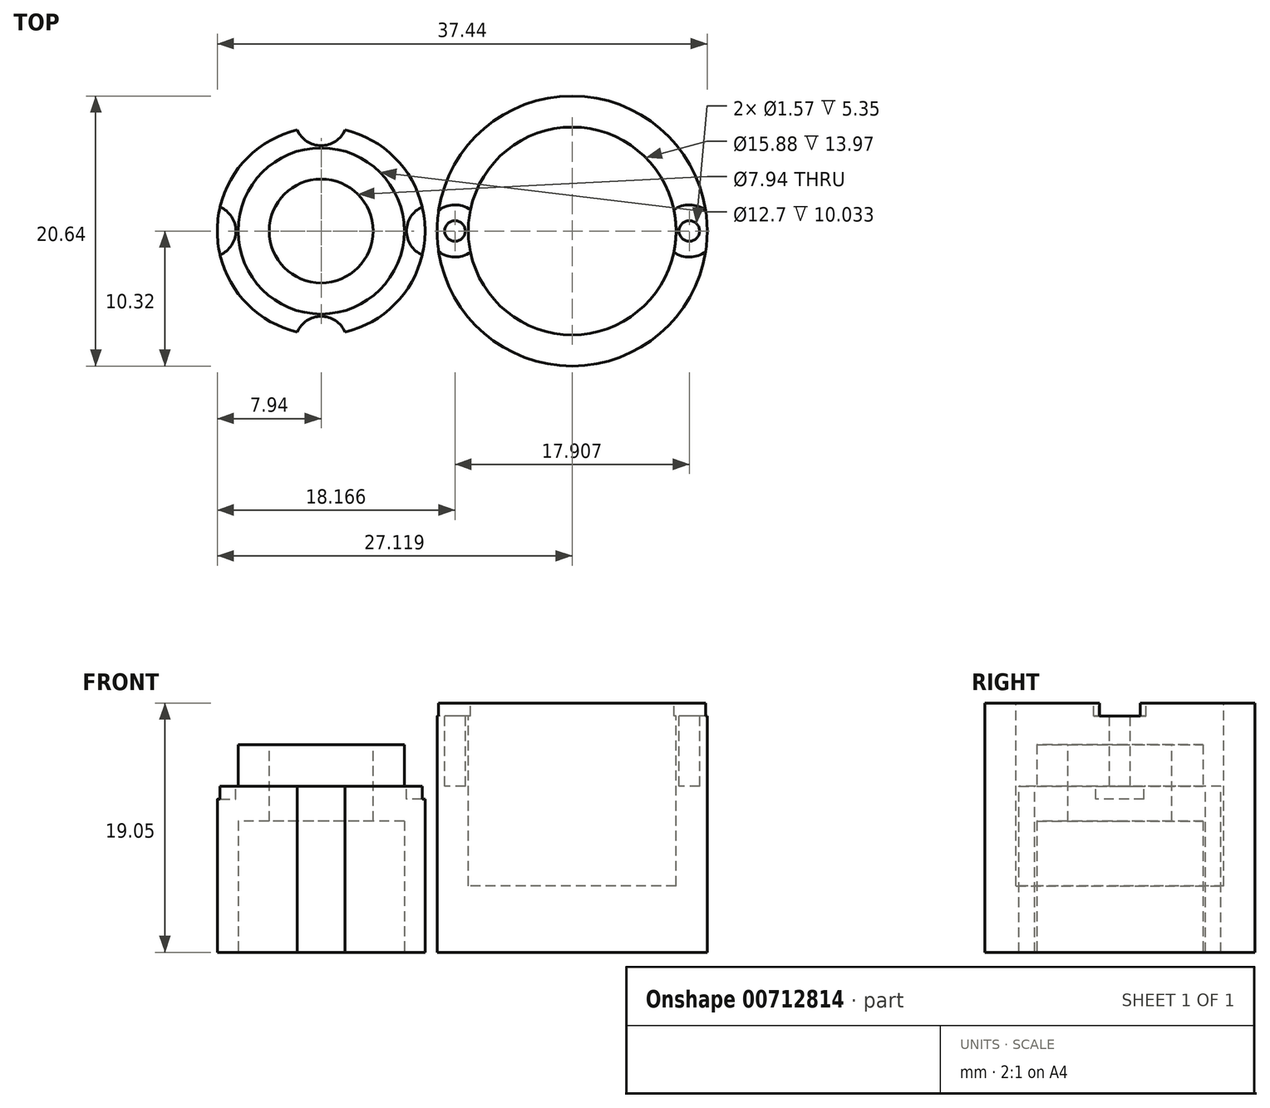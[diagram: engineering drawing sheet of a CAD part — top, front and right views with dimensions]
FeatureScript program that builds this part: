
annotation { "Feature Type Name" : "Feature", "Feature Type Description" : "" }
export const myFeature = defineFeature(function(context is Context, id is Id, definition is map)
    precondition{}
    {
        {
            var Q0;
            Q0=qCreatedBy(makeId("Top.planeOp"),FACE);
            var sketch = newSketch(context, id + "F0", { "sketchPlane" : qUnion([Q0])});
            skCircle(sketch, "E0", {"center": v(0, 0) * mm, "radius": 7.94 * mm});
            skCircle(sketch, "E1", {"center": v(0, 0) * mm, "radius": 6.35 * mm});
            skSolve(sketch);
        }
        {
            var Q0;
            Q0 = qSketchRegion(id + "F0", true);
            var Q1;
            Q1=makeQuery(id+"F0.imprint","IMPRINT",FACE,{"disambiguationData":[TD([[makeQuery(id+"F0.imprint","IMPRINT",EDGE,{"derivedFrom":sQuery(id+"F0.wireOp",EDGE,"E1")}),1.0]])]});
            extrude(context, id + "F1", {"entities" : qUnion([Q0, Q1]), "depth" : 12.7 * mm, "offsetDistance" : 25.4 * mm});
        }
        {
            var Q0;
            Q0=makeQuery(id+"F1.opExtrude","CAP_FACE",FACE,{"disambiguationData":[OSD([sQuery(id+"F0.wireOp",EDGE,"E0")])],"isStart":false});
            var sketch = newSketch(context, id + "F2", { "sketchPlane" : qUnion([Q0])});
            skCircle(sketch, "E2", {"center": v(0, 8.52) * mm, "radius": 2 * mm});
            skCircle(sketch, "E3", {"center": v(8.52, 0) * mm, "radius": 2 * mm});
            skCircle(sketch, "E4", {"center": v(-8.52, 0) * mm, "radius": 2 * mm});
            skCircle(sketch, "E5", {"center": v(0, -8.52) * mm, "radius": 2 * mm});
            skCircle(sketch, "E6", {"center": v(0, 0) * mm, "radius": 6.35 * mm});
            skCircle(sketch, "E7", {"center": v(0, 0) * mm, "radius": 8.52 * mm, "construction": true});
            skSolve(sketch);
        }
        {
            var Q0;
            {var subQ0=sQuery(id+"F2.wireOp",EDGE,"E2");var subQ1=makeQuery(id+"F1.opExtrude","CAP_EDGE",EDGE,{"disambiguationData":[OSD([sQuery(id+"F0.wireOp",EDGE,"E0")])],"isStart":false});var subQ2=makeQuery(id+"F2.imprint","INTERSECT",VERTEX,{"disambiguationData":[OD(0.0)],"derivedFrom":[subQ1,subQ0]});Q0=makeQuery(id+"F2.imprint","IMPRINT",FACE,{"disambiguationData":[TD([[makeQuery(id+"F2.imprint","IMPRINT",EDGE,{"disambiguationData":[TD([[subQ2,-1.0]])],"derivedFrom":subQ0}),1.0]])]});}
            var Q1;
            {var subQ0=sQuery(id+"F2.wireOp",EDGE,"E5");var subQ1=makeQuery(id+"F1.opExtrude","CAP_EDGE",EDGE,{"disambiguationData":[OSD([sQuery(id+"F0.wireOp",EDGE,"E0")])],"isStart":false});var subQ2=makeQuery(id+"F2.imprint","INTERSECT",VERTEX,{"disambiguationData":[OD(0.0)],"derivedFrom":[subQ1,subQ0]});Q1=makeQuery(id+"F2.imprint","IMPRINT",FACE,{"disambiguationData":[TD([[makeQuery(id+"F2.imprint","IMPRINT",EDGE,{"disambiguationData":[TD([[subQ2,1.0]])],"derivedFrom":subQ0}),1.0]])]});}
            extrude(context, id + "F3", {"entities" : qUnion([Q0, Q1]), "operationType" : NewBodyOperationType.REMOVE, "endBound" : BoundingType.THROUGH_ALL, "oppositeDirection" : true, "depth" : 25.4 * mm, "offsetDistance" : 25.4 * mm});
        }
        {
            var Q0;
            {var subQ0=sQuery(id+"F2.wireOp",EDGE,"E4");var subQ1=makeQuery(id+"F1.opExtrude","CAP_EDGE",EDGE,{"disambiguationData":[OSD([sQuery(id+"F0.wireOp",EDGE,"E0")])],"isStart":false});var subQ2=makeQuery(id+"F2.imprint","INTERSECT",VERTEX,{"disambiguationData":[OD(0.0)],"derivedFrom":[subQ1,subQ0]});Q0=makeQuery(id+"F2.imprint","IMPRINT",FACE,{"disambiguationData":[TD([[makeQuery(id+"F2.imprint","IMPRINT",EDGE,{"disambiguationData":[TD([[subQ2,-1.0]])],"derivedFrom":subQ0}),1.0]])]});}
            var Q1;
            {var subQ0=sQuery(id+"F2.wireOp",EDGE,"E3");var subQ1=makeQuery(id+"F1.opExtrude","CAP_EDGE",EDGE,{"disambiguationData":[OSD([sQuery(id+"F0.wireOp",EDGE,"E0")])],"isStart":false});var subQ2=makeQuery(id+"F2.imprint","INTERSECT",VERTEX,{"disambiguationData":[OD(0.0)],"derivedFrom":[subQ1,subQ0]});Q1=makeQuery(id+"F2.imprint","IMPRINT",FACE,{"disambiguationData":[TD([[makeQuery(id+"F2.imprint","IMPRINT",EDGE,{"disambiguationData":[TD([[subQ2,1.0]])],"derivedFrom":subQ0}),1.0]])]});}
            extrude(context, id + "F4", {"entities" : qUnion([Q0, Q1]), "operationType" : NewBodyOperationType.REMOVE, "oppositeDirection" : true, "depth" : 1 * mm, "offsetDistance" : 25.4 * mm});
        }
        {
            var Q0;
            Q0=makeQuery(id+"F2.imprint","IMPRINT",FACE,{"disambiguationData":[TD([[makeQuery(id+"F2.imprint","IMPRINT",EDGE,{"derivedFrom":sQuery(id+"F2.wireOp",EDGE,"E6")}),1.0]])]});
            extrude(context, id + "F5", {"entities" : qUnion([Q0]), "operationType" : NewBodyOperationType.ADD, "depth" : 3.17 * mm, "offsetDistance" : 25.4 * mm});
        }
        {
            var Q0;
            Q0=makeQuery(id+"F5.opExtrude","CAP_FACE",FACE,{"disambiguationData":[OSD([sQuery(id+"F2.wireOp",EDGE,"E6")])],"isStart":false});
            var sketch = newSketch(context, id + "F6", { "sketchPlane" : qUnion([Q0])});
            skPoint(sketch, "E8", {"position": v(0, 0) * mm});
            skSolve(sketch);
        }
        {
            var Q0;
            Q0=sQuery(id+"F6.wireOp",VERTEX,"E8");
            var Q1;
            Q1=makeQuery(id+"F1.opExtrude","SWEPT_BODY",BODY,{"disambiguationData":[OSD([sQuery(id+"F0.wireOp",EDGE,"E0")])]});
            hole(context, id + "F7", {"style" : HoleStyle.SIMPLE, "endStyle" : HoleEndStyle.THROUGH, "holeDiameter" : 7.94 * mm, "majorDiameter" : 6.35 * mm, "isTappedThrough" : true, "tappedDepth" : 12.7 * mm, "tapClearance" : 3, "locations" : qUnion([Q0]), "scope" : qUnion([Q1])});
        }
        {
            var Q0;
            Q0=qCreatedBy(makeId("Top.planeOp"),FACE);
            var sketch = newSketch(context, id + "F8", { "sketchPlane" : qUnion([Q0])});
            skCircle(sketch, "E9", {"center": v(19.18, 0) * mm, "radius": 10.32 * mm});
            skCircle(sketch, "E10", {"center": v(19.18, 0) * mm, "radius": 7.94 * mm});
            skSolve(sketch);
        }
        {
            var Q0;
            Q0=makeQuery(id+"F8.imprint","IMPRINT",FACE,{"disambiguationData":[TD([[makeQuery(id+"F8.imprint","IMPRINT",EDGE,{"derivedFrom":sQuery(id+"F8.wireOp",EDGE,"E9")}),1.0]])]});
            var Q1;
            Q1=makeQuery(id+"F8.imprint","IMPRINT",FACE,{"disambiguationData":[TD([[makeQuery(id+"F8.imprint","IMPRINT",EDGE,{"derivedFrom":sQuery(id+"F8.wireOp",EDGE,"E10")}),1.0]])]});
            extrude(context, id + "F9", {"entities" : qUnion([Q0, Q1]), "depth" : 19.05 * mm, "offsetDistance" : 25.4 * mm});
        }
        {
            var Q0;
            Q0=makeQuery(id+"F9.opExtrude","CAP_FACE",FACE,{"disambiguationData":[OSD([sQuery(id+"F8.wireOp",EDGE,"E9")])],"isStart":false});
            var sketch = newSketch(context, id + "F10", { "sketchPlane" : qUnion([Q0])});
            skCircle(sketch, "E11", {"center": v(19.18, 0) * mm, "radius": 7.94 * mm});
            skCircle(sketch, "E12.0", {"center": v(19.18, 0) * mm, "radius": 8.95 * mm, "construction": true});
            skCircle(sketch, "E13", {"center": v(28.13, 0) * mm, "radius": 0.79 * mm});
            skCircle(sketch, "E14", {"center": v(10.23, 0) * mm, "radius": 0.79 * mm});
            skArc(sketch, "E15", {"start": v(11.4, 1.61) * mm, "mid": v(8.23, 0) * mm, "end": v(11.4, -1.61) * mm});
            skArc(sketch, "E16", {"start": v(26.95, -1.61) * mm, "mid": v(30.13, 0) * mm, "end": v(26.95, 1.61) * mm});
            skSolve(sketch);
        }
        {
            var Q0;
            Q0=makeQuery(id+"F10.imprint","IMPRINT",FACE,{"disambiguationData":[TD([[makeQuery(id+"F10.imprint","IMPRINT",EDGE,{"derivedFrom":sQuery(id+"F10.wireOp",EDGE,"E11")}),1.0]])]});
            extrude(context, id + "F11", {"entities" : qUnion([Q0]), "operationType" : NewBodyOperationType.REMOVE, "oppositeDirection" : true, "depth" : 13.97 * mm, "offsetDistance" : 25.4 * mm});
        }
        {
            var Q0;
            Q0=makeQuery(id+"F10.imprint","IMPRINT",FACE,{"disambiguationData":[TD([[makeQuery(id+"F10.imprint","IMPRINT",EDGE,{"derivedFrom":sQuery(id+"F10.wireOp",EDGE,"E14")}),1.0]])]});
            var Q1;
            Q1=makeQuery(id+"F10.imprint","IMPRINT",FACE,{"disambiguationData":[TD([[makeQuery(id+"F10.imprint","IMPRINT",EDGE,{"derivedFrom":sQuery(id+"F10.wireOp",EDGE,"E13")}),1.0]])]});
            extrude(context, id + "F12", {"entities" : qUnion([Q0, Q1]), "operationType" : NewBodyOperationType.REMOVE, "oppositeDirection" : true, "depth" : 6.35 * mm, "offsetDistance" : 25.4 * mm});
        }
        {
            var Q0;
            Q0=makeQuery(id+"F10.imprint","IMPRINT",FACE,{"disambiguationData":[TD([[makeQuery(id+"F10.imprint","IMPRINT",EDGE,{"derivedFrom":sQuery(id+"F10.wireOp",EDGE,"E14")}),-1.0]])]});
            var Q1;
            Q1=makeQuery(id+"F10.imprint","IMPRINT",FACE,{"disambiguationData":[TD([[makeQuery(id+"F10.imprint","IMPRINT",EDGE,{"derivedFrom":sQuery(id+"F10.wireOp",EDGE,"E13")}),-1.0]])]});
            extrude(context, id + "F13", {"entities" : qUnion([Q0, Q1]), "operationType" : NewBodyOperationType.REMOVE, "oppositeDirection" : true, "depth" : 1 * mm, "offsetDistance" : 25.4 * mm});
        }
        {
            var Q0;
            Q0=makeQuery(id+"F0.imprint","IMPRINT",FACE,{"disambiguationData":[TD([[makeQuery(id+"F0.imprint","IMPRINT",EDGE,{"derivedFrom":sQuery(id+"F0.wireOp",EDGE,"E1")}),1.0]])]});
            extrude(context, id + "F14", {"entities" : qUnion([Q0]), "operationType" : NewBodyOperationType.REMOVE, "depth" : 10.03 * mm, "offsetDistance" : 25.4 * mm});
        }
    });
